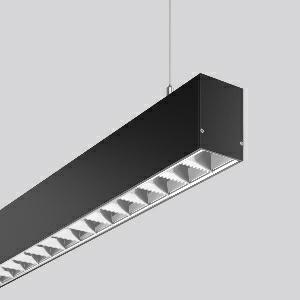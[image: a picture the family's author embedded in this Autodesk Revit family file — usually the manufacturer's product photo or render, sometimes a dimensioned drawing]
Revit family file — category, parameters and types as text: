
# Revit family: less_is_more_50_312335_003_a34b
name_source: partatom
category: Lighting Fixtures
units: mm (PartAtom-declared; Revit-internal decimal feet)

## family parameters
Cut with Voids When Loaded = No
Host = Face
Light Source = No
Part Type = Normal
Room Calculation Point = No
Round Connector Dimension = Use Diameter
Shared = No

## types (1)
- LESS IS MORE 50 (1 x LED Modul 830, 2500 lm, 3000)
    Apparent Load = 22 VA
    CIE Flux Codes = 95 100 100 100 100
    Color Rendering = 80
    Color Temperature = 3000
    Default Elevation = 1800 mm
    Description = Series: LESS IS MORE 50
Linear pendant luminaire for aesthetically sophisticated lighting. Housing: extruded aluminium profile, powder-coated. End cap aluminium powder-coated. Canopy made of aluminium, powder-coated. Alea optical system: Reflector structure (ABS, Aluminium-coated, highly polished) with integrated diffuser made of non-yellowing plastic (PMMA) opal for glare-free light at the workstation (screen-compliant according to EN 12464-1). Direct light emission. Suitable for pendant. 2-point steel cable suspension freely positionable and infinitely height-adjustable. Special lengths available on request. LED unit with integrated converter interchangeable and removable. Suitable for through-wiring. With sensors or as a safety luminaire on request. 
Colour: deep black, matt (RAL 9005)
Length: 847 mm
Width: 57 mm
Height: 75 mm
Suspension length: 2000 mm
Lamp: LED
Socket: without socket
Colour temperature: 3000K
Colour rendering index (CRI): 80
System power: 22 W
Rated luminous flux: 2500 lm
Luminous efficiency: 114 lm/W
Control gear: Regulated power supply
Protection class: I
Type of protection: IP 20
    Height = 75 mm
    Lamp = 1 x LED Modul 830
    Lamp Light Flux = 2500 lm
    Lamp count = 1
    Length = 847 mm
    Lifetime = 50000 h
    Luminous efficacy = 114 lm/W
    Manufacturer = RZB
    ModVariant = No
    Model = 312335.003
    Mounting Place = Ceiling
    Mounting Type = Pendant
    Number of Poles = 1
    OnlyDefault = Yes
    Power Factor = 1
    Product Name = LESS IS MORE 50
    Product group = Pendant LED linear luminaires
    ProductGroupID = 907
    Protection Class = Protection class I
    Protection Degree = IP 20
    RLX_Detail_Level = 1
    RLX_Emergency_Light_Flux = 0 lm
    RLX_Emergency_Type = 0
    RLX_Emergency_Type_DB = No
    RlxData = <blob elided: 39593 chars, md5=16330e66>
    Socket = socket
    Standby Power = 0 W
    System Light Flux = 2500 lm
    System Power = 22 W
    Type Comments = Product without accessories
    Type Image = 312342.003.jpg
    URL = http://relux.com
    VarID = ---
    Voltage = 230 V
    Voltage Range = 220-240 V
    Weight = 0.00 kg
    Width = 57 mm

## geometry (parser evidence)
native form markers: Blend x4, Sweep x10
no freeform markers — native parametric forms only
